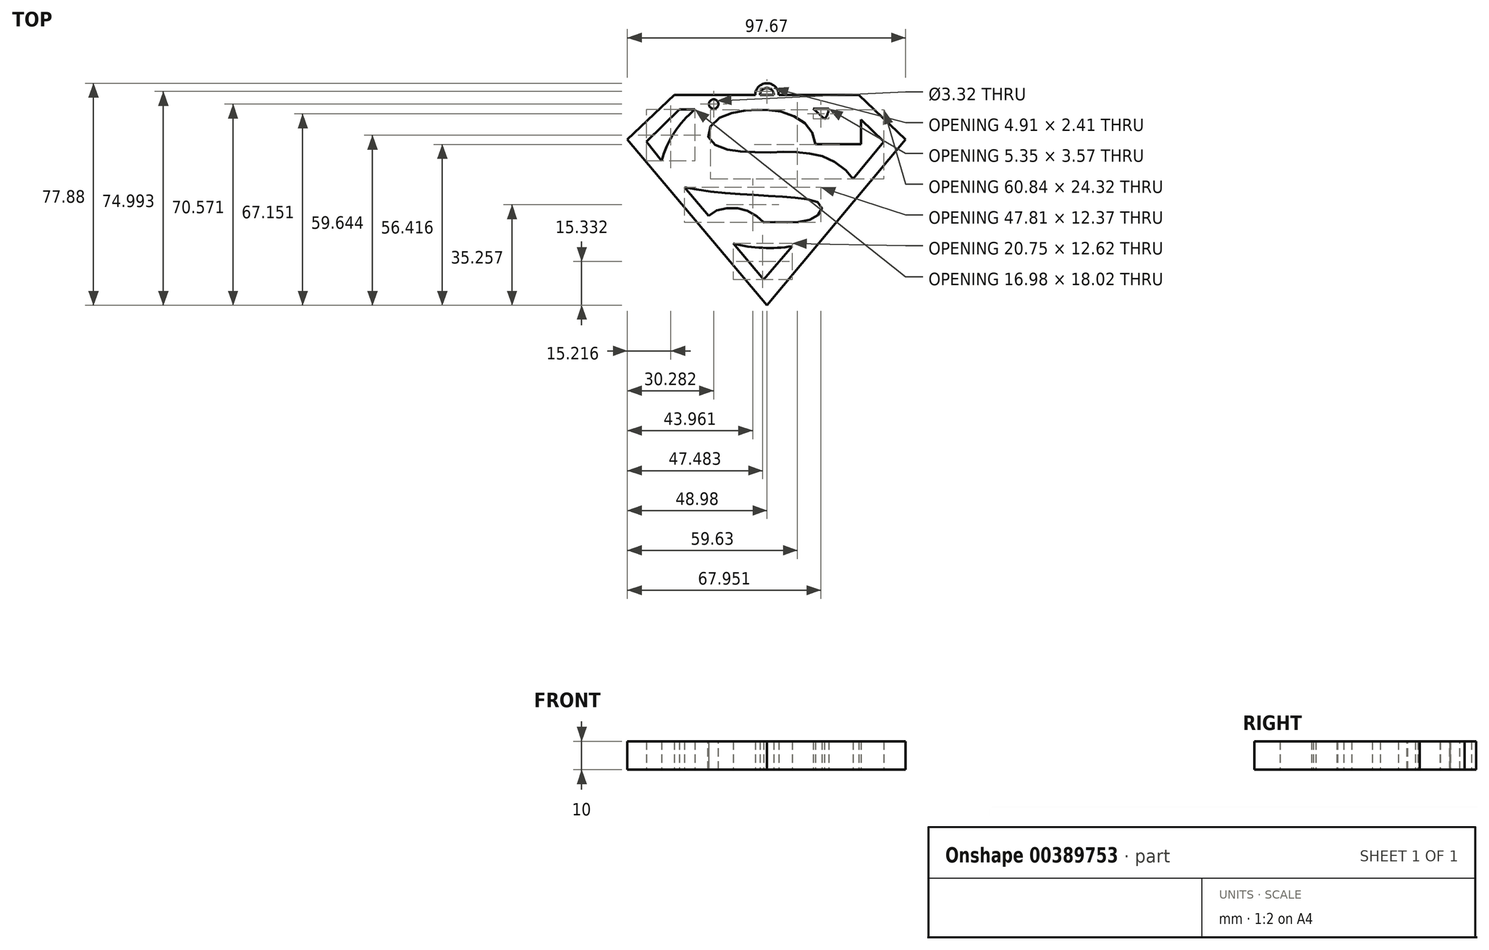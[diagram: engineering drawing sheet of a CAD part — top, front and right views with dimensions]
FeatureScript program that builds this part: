
annotation { "Feature Type Name" : "Feature", "Feature Type Description" : "" }
export const myFeature = defineFeature(function(context is Context, id is Id, definition is map)
    precondition{}
    {
        {
            var Q0;
            Q0=qCreatedBy(makeId("Top.planeOp"),FACE);
            var sketch = newSketch(context, id + "F0", { "sketchPlane" : qUnion([Q0])});
            skLineSegment(sketch, "E0", {"start": v(16.3, 34.83) * mm, "end": v(21.65, 34.83) * mm});
            skLineSegment(sketch, "E1", {"start": v(16.3, 34.83) * mm, "end": v(20.24, 31.27) * mm});
            skArc(sketch, "E2", {"start": v(20.24, 31.27) * mm, "mid": v(21.26, 32.92) * mm, "end": v(21.65, 34.83) * mm});
            skLineSegment(sketch, "E3", {"start": v(33, 31.08) * mm, "end": v(41.07, 23.3) * mm});
            skLineSegment(sketch, "E4", {"start": v(41.07, 23.3) * mm, "end": v(30.18, 10.16) * mm});
            skLineSegment(sketch, "E5", {"start": v(33, 31.08) * mm, "end": v(33, 22.45) * mm});
            skLineSegment(sketch, "E6", {"start": v(33, 22.45) * mm, "end": v(16.95, 22.45) * mm});
            skLineSegment(sketch, "E7", {"start": v(-25.27, 34.55) * mm, "end": v(-30.71, 34.55) * mm});
            skLineSegment(sketch, "E8", {"start": v(-30.71, 34.55) * mm, "end": v(-42.26, 23.3) * mm});
            skLineSegment(sketch, "E9", {"start": v(-42.26, 23.3) * mm, "end": v(-37, 16.54) * mm});
            skArc(sketch, "E10", {"start": v(-25.27, 34.55) * mm, "mid": v(-32.54, 26.46) * mm, "end": v(-37, 16.54) * mm});
            skLineSegment(sketch, "E11", {"start": v(-11.87, -12.46) * mm, "end": v(-1.14, -25.08) * mm});
            skLineSegment(sketch, "E12", {"start": v(-1.14, -25.08) * mm, "end": v(8.88, -13.4) * mm});
            skArc(sketch, "E13", {"start": v(-11.87, -12.46) * mm, "mid": v(-1.54, -13.98) * mm, "end": v(8.88, -13.4) * mm});
            skFitSpline(sketch, "E14", {"points": [v(16.95, 22.45) * mm, v(16.2, 25.88) * mm, v(14.36, 28.84) * mm, v(11.45, 31.19) * mm, v(7.46, 33.06) * mm, v(3.15, 34.1) * mm, v(0, 34.33) * mm, v(-3.23, 34.52) * mm, v(-6.8, 34.33) * mm, v(-11.5, 33.58) * mm, v(-15.34, 32.31) * mm, v(-18.95, 29.87) * mm, v(-20.45, 27.1) * mm, v(-20.45, 24.48) * mm, v(-18.58, 22.45) * mm, v(-14.73, 20.77) * mm, v(-10.65, 19.97) * mm, v(-5.95, 19.7) * mm, v(0, 19.5) * mm, v(4.41, 19.7) * mm, v(8.36, 19.74) * mm, v(12.76, 19.4) * mm, v(16.95, 18.77) * mm, v(20.73, 17.67) * mm, v(25.04, 15.32) * mm, v(28.33, 12.5) * mm, v(30.18, 10.16) * mm], "startDerivative": vector(-14.62, 96.86) * mm, "endDerivative": vector(50.27, -69.68) * mm});
            skLineSegment(sketch, "E15", {"start": v(-28.93, 7.34) * mm, "end": v(-20.48, -2.74) * mm});
            skFitSpline(sketch, "E16", {"points": [v(-28.93, 7.34) * mm, v(-25.17, 6.64) * mm, v(-20.57, 5.94) * mm, v(-15.27, 5.28) * mm, v(-9.69, 4.9) * mm, v(-5, 4.62) * mm, v(0, 4.3) * mm, v(5.14, 3.97) * mm, v(9.08, 3.73) * mm, v(12.78, 3.3) * mm, v(15.93, 2.7) * mm, v(18.32, 1.67) * mm, v(19.21, 0.59) * mm, v(19.21, -0.59) * mm, v(18.27, -2.13) * mm, v(16.58, -3.54) * mm, v(14.33, -4.34) * mm, v(11.05, -4.9) * mm, v(8, -5.09) * mm, v(4.2, -5) * mm, v(0.87, -4.9) * mm, v(-1.8, -4.9) * mm, v(-3.36, -3.17) * mm, v(-5.7, -1.43) * mm, v(-8.1, -0.59) * mm, v(-10.58, 0) * mm, v(-13.68, 0) * mm, v(-16.45, -0.5) * mm, v(-18.46, -1.24) * mm, v(-20.48, -2.74) * mm], "startDerivative": vector(96.25, -18.89) * mm, "endDerivative": vector(-64.66, -54.17) * mm});
            skLineSegment(sketch, "E17", {"start": v(32.23, 39.69) * mm, "end": v(-32.53, 39.69) * mm});
            skLineSegment(sketch, "E18", {"start": v(-32.53, 39.69) * mm, "end": v(-48.98, 24.03) * mm});
            skLineSegment(sketch, "E19", {"start": v(-48.98, 24.03) * mm, "end": v(0, -34.1) * mm});
            skLineSegment(sketch, "E20", {"start": v(0, -34.1) * mm, "end": v(48.69, 24.03) * mm});
            skLineSegment(sketch, "E21", {"start": v(48.69, 24.03) * mm, "end": v(32.23, 39.69) * mm});
            skSolve(sketch);
        }
        {
            var Q0;
            Q0 = qSketchRegion(id + "F0", true);
            extrude(context, id + "F1", {"entities" : qUnion([Q0]), "depth" : 10 * mm});
        }
        {
            var Q0;
            Q0=qCreatedBy(makeId("Top.planeOp"),FACE);
            var sketch = newSketch(context, id + "F2", { "sketchPlane" : qUnion([Q0])});
            skCircle(sketch, "E22", {"center": v(0, 39.65) * mm, "radius": 4.13 * mm});
            skCircle(sketch, "E23", {"center": v(0, 39.65) * mm, "radius": 2.45 * mm});
            skSolve(sketch);
        }
        {
            var Q0;
            Q0 = qSketchRegion(id + "F2", true);
            extrude(context, id + "F3", {"entities" : qUnion([Q0]), "operationType" : NewBodyOperationType.ADD, "depth" : 10 * mm});
        }
        {
            var Q0;
            Q0=makeQuery(id+"F3.boolean.opBoolean","MERGE",FACE,{"derivedFrom":[makeQuery(id+"F1.opExtrude","CAP_FACE",FACE,{"disambiguationData":[OSD([sQuery(id+"F0.wireOp",EDGE,"E0"),sQuery(id+"F0.wireOp",EDGE,"E1"),sQuery(id+"F0.wireOp",EDGE,"E2"),sQuery(id+"F0.wireOp",EDGE,"E3"),sQuery(id+"F0.wireOp",EDGE,"E4"),sQuery(id+"F0.wireOp",EDGE,"E5"),sQuery(id+"F0.wireOp",EDGE,"E6"),sQuery(id+"F0.wireOp",EDGE,"E7"),sQuery(id+"F0.wireOp",EDGE,"E8"),sQuery(id+"F0.wireOp",EDGE,"E9"),sQuery(id+"F0.wireOp",EDGE,"E10"),sQuery(id+"F0.wireOp",EDGE,"E11"),sQuery(id+"F0.wireOp",EDGE,"E12"),sQuery(id+"F0.wireOp",EDGE,"E13"),sQuery(id+"F0.wireOp",EDGE,"E14"),sQuery(id+"F0.wireOp",EDGE,"E15"),sQuery(id+"F0.wireOp",EDGE,"E16"),sQuery(id+"F0.wireOp",EDGE,"E17"),sQuery(id+"F0.wireOp",EDGE,"E18"),sQuery(id+"F0.wireOp",EDGE,"E19"),sQuery(id+"F0.wireOp",EDGE,"E20"),sQuery(id+"F0.wireOp",EDGE,"E21")])],"isStart":false}),makeQuery(id+"F3.opExtrude","CAP_FACE",FACE,{"disambiguationData":[OSD([sQuery(id+"F2.wireOp",EDGE,"E22"),sQuery(id+"F2.wireOp",EDGE,"E23")])],"isStart":false})]});
            var sketch = newSketch(context, id + "F4", { "sketchPlane" : qUnion([Q0])});
            skCircle(sketch, "E24", {"center": v(-18.7, 36.47) * mm, "radius": 1.66 * mm});
            skSolve(sketch);
        }
        {
            var Q0;
            Q0 = qSketchRegion(id + "F4", true);
            var Q1;
            Q1=makeQuery(id+"F3.boolean.opBoolean","MERGE",FACE,{"derivedFrom":[makeQuery(id+"F1.opExtrude","CAP_FACE",FACE,{"disambiguationData":[OSD([sQuery(id+"F0.wireOp",EDGE,"E0"),sQuery(id+"F0.wireOp",EDGE,"E1"),sQuery(id+"F0.wireOp",EDGE,"E2"),sQuery(id+"F0.wireOp",EDGE,"E3"),sQuery(id+"F0.wireOp",EDGE,"E4"),sQuery(id+"F0.wireOp",EDGE,"E5"),sQuery(id+"F0.wireOp",EDGE,"E6"),sQuery(id+"F0.wireOp",EDGE,"E7"),sQuery(id+"F0.wireOp",EDGE,"E8"),sQuery(id+"F0.wireOp",EDGE,"E9"),sQuery(id+"F0.wireOp",EDGE,"E10"),sQuery(id+"F0.wireOp",EDGE,"E11"),sQuery(id+"F0.wireOp",EDGE,"E12"),sQuery(id+"F0.wireOp",EDGE,"E13"),sQuery(id+"F0.wireOp",EDGE,"E14"),sQuery(id+"F0.wireOp",EDGE,"E15"),sQuery(id+"F0.wireOp",EDGE,"E16"),sQuery(id+"F0.wireOp",EDGE,"E17"),sQuery(id+"F0.wireOp",EDGE,"E18"),sQuery(id+"F0.wireOp",EDGE,"E19"),sQuery(id+"F0.wireOp",EDGE,"E20"),sQuery(id+"F0.wireOp",EDGE,"E21")])],"isStart":true}),makeQuery(id+"F3.opExtrude","CAP_FACE",FACE,{"disambiguationData":[OSD([sQuery(id+"F2.wireOp",EDGE,"E22"),sQuery(id+"F2.wireOp",EDGE,"E23")])],"isStart":true})]});
            extrude(context, id + "F5", {"entities" : qUnion([Q0]), "operationType" : NewBodyOperationType.REMOVE, "endBound" : BoundingType.UP_TO_SURFACE, "oppositeDirection" : true, "endBoundEntityFace" : qUnion([Q1]), "depth" : 25 * mm});
        }
    });
